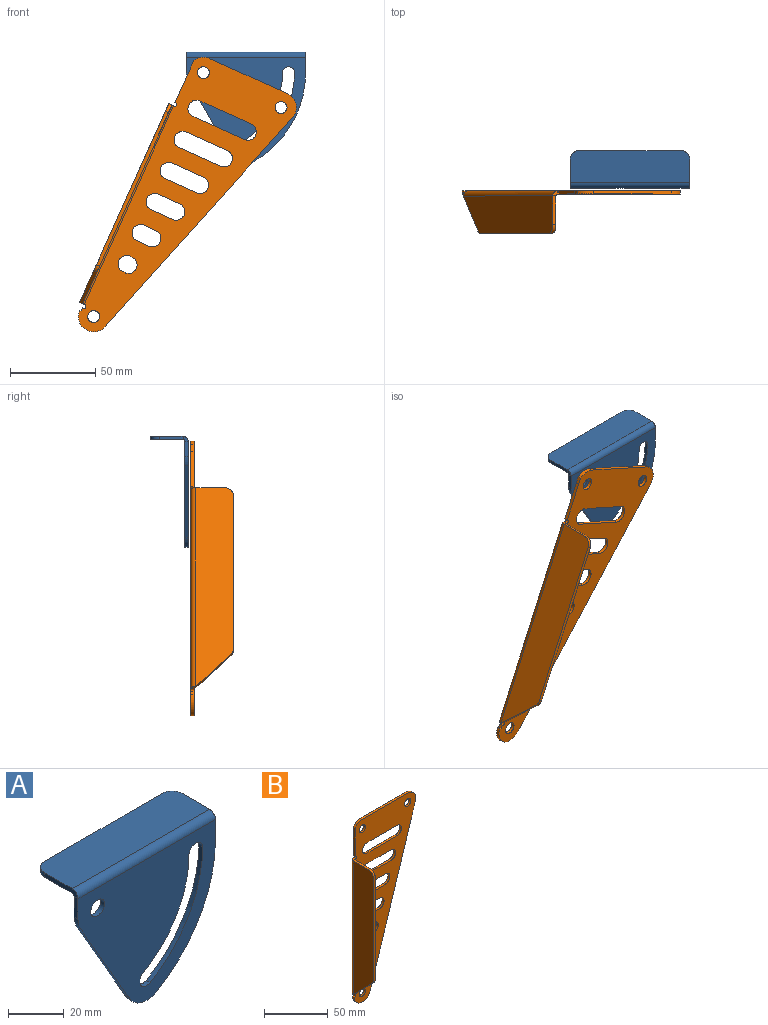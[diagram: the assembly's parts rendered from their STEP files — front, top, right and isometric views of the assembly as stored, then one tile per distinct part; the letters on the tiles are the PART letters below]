
ASSEMBLY  parts=2 mates=1
PART A: 27 faces, bbox 70x22x65.3 mm
  f0: cylinder r=60mm len=51.96mm, axis (0,-1,0), area 125.7mm2, adj f1,f13,f14,f15
  f1: plane 9x2mm, normal (1,0,0), area 18mm2, adj f0,f14,f15,f24
  f2: plane 9x2mm, normal (-1,0,0), area 18mm2, adj f3,f14,f15,f23
  f3: cylinder r=10mm len=5.01mm, axis (0,-1,0), area 10.5mm2, adj f2,f4,f14,f15
  f4: plane 42.41x24.52mm, normal (-0.87,0,-0.5), area 98mm2, adj f3,f5,f14,f15
  f5: cylinder r=50mm len=2mm, axis (0,-1,0), area 0mm2, adj f4,f6,f14,f15
  f6: cylinder r=10mm len=2mm, axis (0,-1,0), area 0.5mm2, adj f5,f7,f14,f15
  f7: plane 2x1.3mm, normal (-0.87,0,-0.5), area 3mm2, adj f6,f13,f14,f15
  f8: cylinder r=53.5mm len=46.33mm, axis (0,-1,0), area 112.1mm2, adj f9,f12,f14,f15
  f9: cylinder r=3.5mm len=6.53mm, axis (0,-1,0), area 22mm2, adj f8,f10,f14,f15
  f10: cylinder r=46.5mm len=40.27mm, axis (0,-1,0), area 97.4mm2, adj f9,f12,f14,f15
  f11: cylinder r=3.5mm len=7mm, axis (0,-1,0), area 44mm2, adj f14,f15
  f12: cylinder r=3.5mm len=7mm, axis (0,-1,0), area 22mm2, adj f8,f10,f14,f15
  f13: cylinder r=10mm len=13.26mm, axis (0,-1,0), area 29.9mm2, adj f0,f7,f14,f15
  f14: plane 70x62.3mm, normal (0,-1,0), area 2675.5mm2, adj f0,f1,f2,f3,f4,f5,f6,f7
  f15: plane 70x62.3mm, normal (0,1,0), area 2675.5mm2, adj f0,f1,f2,f3,f4,f5,f6,f7
  f16: plane 60x2mm, normal (0,1,0), area 120mm2, adj f19,f20,f21,f22
  f17: plane 14x2mm, normal (-1,0,0), area 28mm2, adj f19,f20,f22,f23
  f18: plane 14x2mm, normal (1,0,0), area 28mm2, adj f19,f20,f21,f24
  f19: plane 70x19mm, normal (0,0,1), area 1319.3mm2, adj f16,f17,f18,f21,f22,f25
  f20: plane 70x19mm, normal (0,0,-1), area 1319.3mm2, adj f16,f17,f18,f21,f22,f26
  f21: cylinder r=5mm len=5mm, axis (0,0,1), area 15.7mm2, adj f16,f18,f19,f20
  f22: cylinder r=5mm len=5mm, axis (0,0,-1), area 15.7mm2, adj f16,f17,f19,f20
  f23: plane 3x3mm, normal (-1,0,0), area 6.3mm2, adj f2,f17,f25,f26
  f24: plane 3x3mm, normal (1,0,0), area 6.3mm2, adj f1,f18,f25,f26
  f25: cylinder r=3mm len=70mm, axis (-1,0,0), area 329.9mm2, adj f14,f19,f23,f24
  f26: cylinder r=1mm len=70mm, axis (-1,0,0), area 110mm2, adj f15,f20,f23,f24
PART B: 55 faces, bbox 70x25x175 mm
  f0: plane 22.88x2mm, normal (-1,0,0), area 45.8mm2, adj f2,f3,f18,f41
  f1: plane 2x2mm, normal (-1,0,0), area 4mm2, adj f2,f3,f4,f40
  f2: plane 175x68mm, normal (0,1,0), area 5745mm2, adj f0,f1,f4,f5,f6,f7,f8,f9
  f3: plane 175x68mm, normal (0,-1,0), area 5745mm2, adj f0,f1,f4,f5,f6,f7,f8,f9
  f4: plane 2x1mm, normal (0,0,1), area 2mm2, adj f1,f2,f3,f13
  f5: plane 20.33x2mm, normal (0,0,1), area 40.7mm2, adj f2,f3,f28,f29
  f6: plane 13.96x2mm, normal (0,0,1), area 27.9mm2, adj f2,f3,f26,f27
  f7: plane 7.59x2mm, normal (0,0,1), area 15.2mm2, adj f2,f3,f30,f32
  f8: plane 2x1.22mm, normal (0,0,1), area 2.4mm2, adj f2,f3,f36,f37
  f9: cylinder r=9mm len=8mm, axis (0,-1,0), area 19.7mm2, adj f2,f3,f10,f18
  f10: plane 50x2mm, normal (0,0,1), area 100mm2, adj f2,f3,f9,f11
  f11: cylinder r=9mm len=11.73mm, axis (0,-1,0), area 33.8mm2, adj f2,f3,f10,f12
  f12: plane 157x50mm, normal (0.95,0,-0.3), area 329.5mm2, adj f2,f3,f11,f13
  f13: cylinder r=9mm len=17.58mm, axis (0,-1,0), area 51mm2, adj f2,f3,f4,f12
  f14: plane 26.7x2mm, normal (0,0,1), area 53.4mm2, adj f2,f3,f34,f35
  f15: plane 26.7x2mm, normal (0,0,-1), area 53.4mm2, adj f2,f3,f34,f35
  f16: plane 33.06x2mm, normal (0,0,1), area 66.1mm2, adj f2,f3,f31,f33
  f17: plane 33.06x2mm, normal (0,0,-1), area 66.1mm2, adj f2,f3,f31,f33
  f18: plane 4.12x2mm, normal (-1,0,0), area 8.2mm2, adj f0,f2,f3,f9
  f19: cylinder r=3.5mm len=7mm, axis (0,-1,0), area 44mm2, adj f2,f3
  f20: plane 2x1.22mm, normal (0,0,-1), area 2.4mm2, adj f2,f3,f36,f37
  f21: plane 7.59x2mm, normal (0,0,-1), area 15.2mm2, adj f2,f3,f30,f32
  f22: plane 13.96x2mm, normal (0,0,-1), area 27.9mm2, adj f2,f3,f26,f27
  f23: plane 20.33x2mm, normal (0,0,-1), area 40.7mm2, adj f2,f3,f28,f29
  f24: cylinder r=3.5mm len=7mm, axis (0,-1,0), area 44mm2, adj f2,f3
  f25: cylinder r=3.5mm len=7mm, axis (0,-1,0), area 44mm2, adj f2,f3
  f26: cylinder r=5mm len=10mm, axis (0,1,0), area 31.4mm2, adj f2,f3,f6,f22
  f27: cylinder r=5mm len=10mm, axis (0,1,0), area 31.4mm2, adj f2,f3,f6,f22
  f28: cylinder r=5mm len=10mm, axis (0,1,0), area 31.4mm2, adj f2,f3,f5,f23
  f29: cylinder r=5mm len=10mm, axis (0,1,0), area 31.4mm2, adj f2,f3,f5,f23
  f30: cylinder r=5mm len=10mm, axis (0,-1,0), area 31.4mm2, adj f2,f3,f7,f21
  f31: cylinder r=5mm len=10mm, axis (0,-1,0), area 31.4mm2, adj f2,f3,f16,f17
  f32: cylinder r=5mm len=10mm, axis (0,-1,0), area 31.4mm2, adj f2,f3,f7,f21
  f33: cylinder r=5mm len=10mm, axis (0,-1,0), area 31.4mm2, adj f2,f3,f16,f17
  f34: cylinder r=5mm len=10mm, axis (0,-1,0), area 31.4mm2, adj f2,f3,f14,f15
  f35: cylinder r=5mm len=10mm, axis (0,1,0), area 31.4mm2, adj f2,f3,f14,f15
  f36: cylinder r=5mm len=10mm, axis (0,-1,0), area 31.4mm2, adj f2,f3,f8,f20
  f37: cylinder r=5mm len=10mm, axis (0,-1,0), area 31.4mm2, adj f2,f3,f8,f20
  f38: plane 2x0.44mm, normal (0,0,-1), area 0.9mm2, adj f2,f3,f39,f51
  f39: cylinder r=1.06mm len=2.13mm, axis (0,-1,0), area 6.7mm2, adj f2,f3,f38,f40
  f40: plane 2x0.44mm, normal (0,0,1), area 0.9mm2, adj f1,f2,f3,f39
  f41: plane 2x0.44mm, normal (0,0,-1), area 0.9mm2, adj f0,f2,f3,f42
  f42: cylinder r=1.06mm len=2.13mm, axis (0,-1,0), area 6.7mm2, adj f2,f3,f41,f43
  f43: plane 2x0.44mm, normal (0,0,1), area 0.9mm2, adj f2,f3,f42,f52
  f44: plane 98.81x2mm, normal (0,-1,0), area 197.6mm2, adj f47,f48,f49,f50
  f45: plane 17x2mm, normal (0,0,1), area 34mm2, adj f47,f48,f49,f52
  f46: plane 20.54x20.54mm, normal (0,-0.71,-0.71), area 58.1mm2, adj f47,f48,f50,f51
  f47: plane 127.88x22mm, normal (-1,0,0), area 2565.4mm2, adj f44,f45,f46,f49,f50,f53
  f48: plane 127.88x22mm, normal (1,0,0), area 2565.4mm2, adj f44,f45,f46,f49,f50,f54
  f49: cylinder r=5mm len=5mm, axis (1,0,0), area 15.7mm2, adj f44,f45,f47,f48
  f50: cylinder r=5mm len=3.54mm, axis (1,0,0), area 7.9mm2, adj f44,f46,f47,f48
  f51: plane 3x3mm, normal (0,0,-1), area 6.3mm2, adj f38,f46,f53,f54
  f52: plane 3x3mm, normal (0,0,1), area 6.3mm2, adj f43,f45,f53,f54
  f53: cylinder r=3mm len=127.88mm, axis (0,0,-1), area 602.6mm2, adj f2,f47,f51,f52
  f54: cylinder r=1mm len=127.88mm, axis (0,0,-1), area 200.9mm2, adj f3,f48,f51,f52
PLACE A t=(161.06,0.89,-72.62)mm
PLACE B rot(axis=(0,1,0),24.2deg) t=(138.36,-2.61,-78.47)mm
MATE revolute B.f9 <-> A.f0  axis (0,-1,0) through (136.06,-13.61,-22.62)mm
